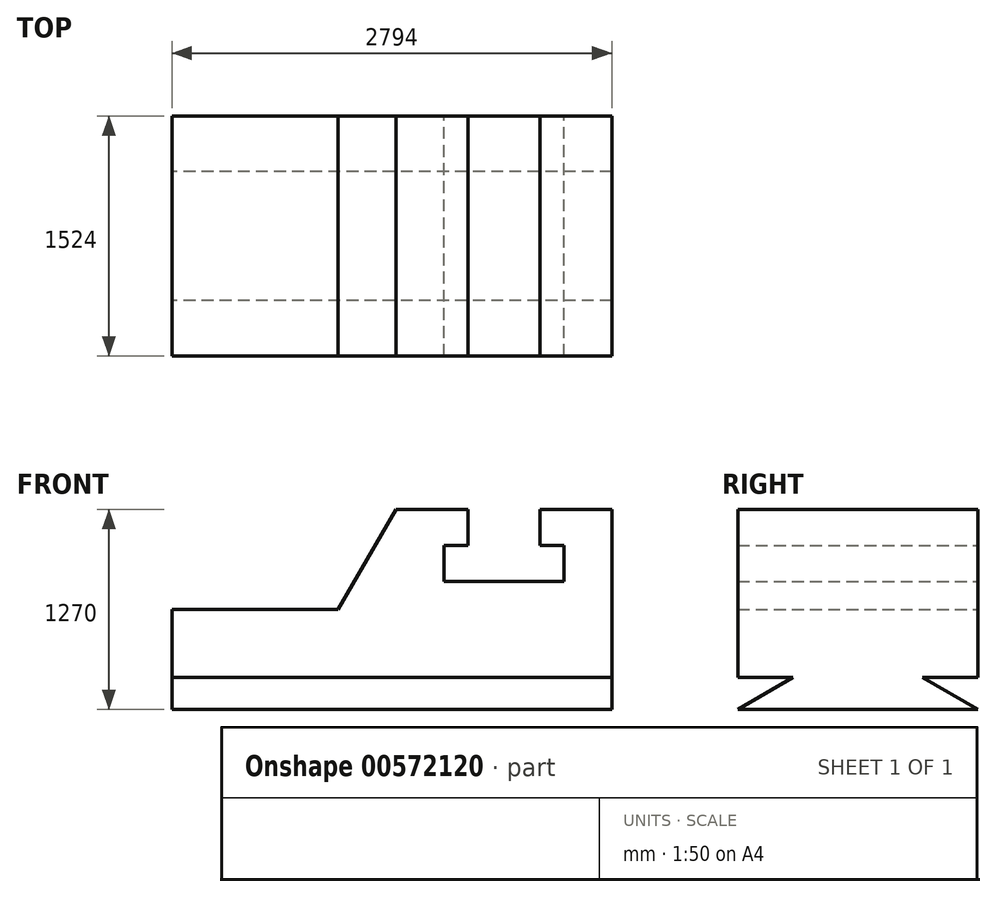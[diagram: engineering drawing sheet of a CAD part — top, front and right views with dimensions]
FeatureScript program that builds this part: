
annotation { "Feature Type Name" : "Feature", "Feature Type Description" : "" }
export const myFeature = defineFeature(function(context is Context, id is Id, definition is map)
    precondition{}
    {
        {
            var Q0;
            Q0=qCreatedBy(makeId("Front.planeOp"),FACE);
            var sketch = newSketch(context, id + "F0", { "sketchPlane" : qUnion([Q0])});
            skLineSegment(sketch, "E0", {"start": v(0, 0) * mm, "end": v(0, -635) * mm});
            skLineSegment(sketch, "E1", {"start": v(0, -635) * mm, "end": v(2794, -635) * mm});
            skLineSegment(sketch, "E2", {"start": v(2794, -635) * mm, "end": v(2794, 635) * mm});
            skLineSegment(sketch, "E3", {"start": v(1422.4, 635) * mm, "end": v(1055.78, 0) * mm});
            skLineSegment(sketch, "E4", {"start": v(0, 0) * mm, "end": v(1055.78, 0) * mm});
            skLineSegment(sketch, "E5", {"start": v(1422.4, 635) * mm, "end": v(1879.6, 635) * mm});
            skLineSegment(sketch, "E6", {"start": v(2794, 635) * mm, "end": v(2336.8, 635) * mm});
            skLineSegment(sketch, "E7", {"start": v(2336.8, 635) * mm, "end": v(2336.8, 406.4) * mm});
            skLineSegment(sketch, "E8", {"start": v(2336.8, 406.4) * mm, "end": v(2489.2, 406.4) * mm});
            skLineSegment(sketch, "E9", {"start": v(2489.2, 406.4) * mm, "end": v(2489.2, 177.8) * mm});
            skLineSegment(sketch, "E10", {"start": v(2489.2, 177.8) * mm, "end": v(1727.2, 177.8) * mm});
            skLineSegment(sketch, "E11", {"start": v(1727.2, 177.8) * mm, "end": v(1727.2, 406.4) * mm});
            skLineSegment(sketch, "E12", {"start": v(1727.2, 406.4) * mm, "end": v(1879.6, 406.4) * mm});
            skLineSegment(sketch, "E13", {"start": v(1879.6, 406.4) * mm, "end": v(1879.6, 635) * mm});
            skSolve(sketch);
        }
        {
            var Q0;
            Q0=makeQuery(id+"F0.imprint","IMPRINT",FACE,{"disambiguationData":[TD([[makeQuery(id+"F0.imprint","IMPRINT",EDGE,{"derivedFrom":sQuery(id+"F0.wireOp",EDGE,"E0")}),1.0]])]});
            extrude(context, id + "F1", {"entities" : qUnion([Q0]), "depth" : 1524 * mm, "offsetDistance" : 25.4 * mm});
        }
        {
            var Q0;
            Q0=makeQuery(id+"F1.opExtrude","SWEPT_FACE",FACE,{"disambiguationData":[OSD([sQuery(id+"F0.wireOp",EDGE,"E0")])]});
            var sketch = newSketch(context, id + "F2", { "sketchPlane" : qUnion([Q0])});
            skLineSegment(sketch, "E14", {"start": v(0, -635) * mm, "end": v(0, -431.8) * mm});
            skLineSegment(sketch, "E15", {"start": v(0, -635) * mm, "end": v(351.95, -431.8) * mm});
            skLineSegment(sketch, "E16", {"start": v(351.95, -431.8) * mm, "end": v(0, -431.8) * mm});
            skLineSegment(sketch, "E17", {"start": v(1524, -635) * mm, "end": v(1524, -431.8) * mm});
            skLineSegment(sketch, "E18", {"start": v(1524, -635) * mm, "end": v(1172.05, -431.8) * mm});
            skLineSegment(sketch, "E19", {"start": v(1172.05, -431.8) * mm, "end": v(1524, -431.8) * mm});
            skSolve(sketch);
        }
        {
            var Q0;
            Q0=makeQuery(id+"F2.imprint","IMPRINT",FACE,{"disambiguationData":[TD([[makeQuery(id+"F2.imprint","IMPRINT",EDGE,{"derivedFrom":sQuery(id+"F2.wireOp",EDGE,"E14")}),1.0]])]});
            var Q1;
            Q1=makeQuery(id+"F2.imprint","IMPRINT",FACE,{"disambiguationData":[TD([[makeQuery(id+"F2.imprint","IMPRINT",EDGE,{"derivedFrom":sQuery(id+"F2.wireOp",EDGE,"E17")}),-1.0]])]});
            extrude(context, id + "F3", {"entities" : qUnion([Q0, Q1]), "operationType" : NewBodyOperationType.REMOVE, "endBound" : BoundingType.THROUGH_ALL, "oppositeDirection" : true, "depth" : 25.4 * mm, "offsetDistance" : 25.4 * mm});
        }
    });
